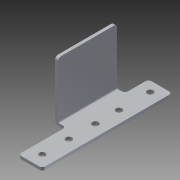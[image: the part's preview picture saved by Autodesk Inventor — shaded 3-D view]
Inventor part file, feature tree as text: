
AUTODESK INVENTOR PART (.ipt)
format: ipt  version: 2013 (Build 170138000, 138)  size: 244,224 bytes
history: native  units: in
note: dims shown in document units (in); Inventor stores cm internally (conversion verified against a paired STEP export)
features: sheet_metal_op x4, other x4, sketch x3, chamfer x1, reference x1
ambient origin geometry x8: Origin, YZ Plane, XZ Plane, XY Plane, X Axis, Y Axis, Z Axis, Center Point
bodies: Solid1 (feature_tree)
feature tree (13):
  sheet_metal_op  "Face1"
  sheet_metal_op  "Flange1"
  chamfer  "Corner Round1"
  sketch  "Sketch1"  dims[d0=1.0in]
  other  "Plate1"
  sketch  "Sketch2"  dims[d1=5.5in]
  other  "Plate2"
  sheet_metal_op  "Bend1"
  sheet_metal_op  "Corner1"
  sketch  "Sketch3"  dims[d2=0.5in d3=1.125in d4=1.125in d5=1.0in d6=1.325in d7=0.26in d8=2.5in d9=0.454in d10=2.0in d11=0.125in d12=0.125in d13=0.0625in d14=0.25in d15=0.125in d16=2.75in d17=90.0deg d18=0.05in d19=0.5in d20=0.125in d21=0.125in d22=0.125in d23=0.266in d25=0.266in d26=0.125in d27=0.0in d28=0.625in d29=0.7874in d31=1.0in d32=0.7874in d34=1.5in d37=0.5in d38=0.625in]
  reference  "Reference1"
  other  "Cut1"
  other  "Definition1"
